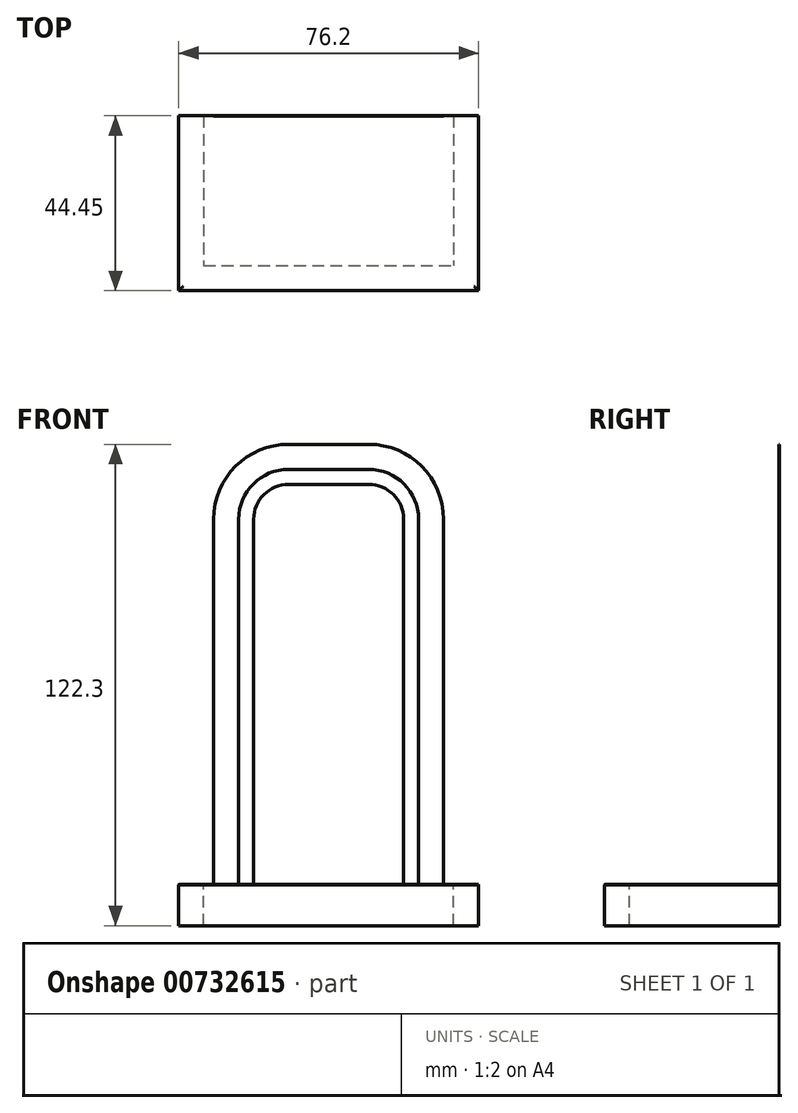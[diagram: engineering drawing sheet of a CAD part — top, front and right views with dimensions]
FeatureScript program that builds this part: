
annotation { "Feature Type Name" : "Feature", "Feature Type Description" : "" }
export const myFeature = defineFeature(function(context is Context, id is Id, definition is map)
    precondition{}
    {
        {
            assignVariable(context, id + "F0", {"name" : "t", "anyValue" : .125});
        }
        {
            var Q0;
            Q0=qCreatedBy(makeId("Front.planeOp"),FACE);
            var sketch = newSketch(context, id + "F1", { "sketchPlane" : qUnion([Q0])});
            skLineSegment(sketch, "E0.bottom", {"start": v(19.05, 111.76) * mm, "end": v(39.37, 111.76) * mm});
            skLineSegment(sketch, "E0.top", {"start": v(0, 0) * mm, "end": v(6.35, 0) * mm});
            skLineSegment(sketch, "E0.left", {"start": v(0, 92.71) * mm, "end": v(0, 0) * mm});
            skLineSegment(sketch, "E0.right", {"start": v(58.42, 92.71) * mm, "end": v(58.42, 0) * mm});
            skPoint(sketch, "E1.visualSharp", {"position": v(0, 111.76) * mm});
            skArc(sketch, "E1.filletArc", {"start": v(19.05, 111.76) * mm, "mid": v(5.58, 106.18) * mm, "end": v(0, 92.71) * mm});
            skPoint(sketch, "E2.visualSharp", {"position": v(58.42, 111.76) * mm});
            skArc(sketch, "E2.filletArc", {"start": v(58.42, 92.71) * mm, "mid": v(52.84, 106.18) * mm, "end": v(39.37, 111.76) * mm});
            skLineSegment(sketch, "E3.0", {"start": v(52.07, 92.71) * mm, "end": v(52.07, 0) * mm});
            skLineSegment(sketch, "E3.1", {"start": v(6.35, 92.71) * mm, "end": v(6.35, 0) * mm});
            skArc(sketch, "E3.2", {"start": v(19.05, 105.41) * mm, "mid": v(10.07, 101.7) * mm, "end": v(6.35, 92.71) * mm});
            skLineSegment(sketch, "E3.3", {"start": v(19.05, 105.41) * mm, "end": v(39.37, 105.41) * mm});
            skArc(sketch, "E3.4", {"start": v(52.07, 92.71) * mm, "mid": v(48.35, 101.7) * mm, "end": v(39.37, 105.41) * mm});
            skLineSegment(sketch, "E4.trimOffspring", {"start": v(52.07, 0) * mm, "end": v(58.42, 0) * mm});
            skSolve(sketch);
        }
        {
            var Q0;
            Q0 = qSketchRegion(id + "F1", true);
            extrude(context, id + "F2", {"entities" : qUnion([Q0]), "depth" : (getVariable(context, 't')) * mm, "offsetDistance" : 25.4 * mm});
        }
        {
            var Q0;
            Q0=qCreatedBy(makeId("Top.planeOp"),FACE);
            var sketch = newSketch(context, id + "F3", { "sketchPlane" : qUnion([Q0])});
            skLineSegment(sketch, "E5.bottom", {"start": v(-8.9, 0) * mm, "end": v(67.3, 0) * mm});
            skLineSegment(sketch, "E5.top", {"start": v(-8.9, -44.45) * mm, "end": v(67.3, -44.45) * mm});
            skLineSegment(sketch, "E5.left", {"start": v(-8.9, 0) * mm, "end": v(-8.9, -44.45) * mm});
            skLineSegment(sketch, "E5.right", {"start": v(67.3, 0) * mm, "end": v(67.31, -44.45) * mm});
            skPoint(sketch, "E6", {"position": v(29.2, 0) * mm});
            skSolve(sketch);
        }
        {
            var Q0;
            Q0 = qSketchRegion(id + "F3", true);
            extrude(context, id + "F4", {"entities" : qUnion([Q0]), "operationType" : NewBodyOperationType.ADD, "oppositeDirection" : true, "depth" : (getVariable(context, 't')) * mm, "offsetDistance" : 25.4 * mm});
        }
        {
            var Q0;
            Q0=qCreatedBy(makeId("Front.planeOp"),FACE);
            var sketch = newSketch(context, id + "F5", { "sketchPlane" : qUnion([Q0])});
            skLineSegment(sketch, "E7.bottom", {"start": v(19.05, 101.6) * mm, "end": v(39.37, 101.6) * mm});
            skLineSegment(sketch, "E7.top", {"start": v(10.16, 0) * mm, "end": v(48.26, 0) * mm});
            skLineSegment(sketch, "E7.left", {"start": v(10.16, 92.71) * mm, "end": v(10.16, 0) * mm});
            skLineSegment(sketch, "E7.right", {"start": v(48.26, 92.71) * mm, "end": v(48.26, 0) * mm});
            skPoint(sketch, "E8.visualSharp", {"position": v(10.16, 101.6) * mm});
            skArc(sketch, "E8.filletArc", {"start": v(19.05, 101.6) * mm, "mid": v(12.76, 99) * mm, "end": v(10.16, 92.71) * mm});
            skPoint(sketch, "E9.visualSharp", {"position": v(48.26, 101.6) * mm});
            skArc(sketch, "E9.filletArc", {"start": v(48.26, 92.71) * mm, "mid": v(45.66, 99) * mm, "end": v(39.37, 101.6) * mm});
            skPoint(sketch, "E10", {"position": v(29.21, 0) * mm});
            skLineSegment(sketch, "E11.0.1", {"start": v(58.42, 0) * mm, "end": v(52.07, 0) * mm});
            skLineSegment(sketch, "E11.0.3", {"start": v(52.07, 0) * mm, "end": v(6.35, 0) * mm});
            skLineSegment(sketch, "E11.0.5", {"start": v(6.35, 0) * mm, "end": v(0, 0) * mm});
            skLineSegment(sketch, "E11.0.7", {"start": v(0, 0) * mm, "end": v(-8.9, 0) * mm});
            skLineSegment(sketch, "E11.0.9", {"start": v(-8.9, 0) * mm, "end": v(67.31, 0) * mm});
            skLineSegment(sketch, "E11.0.11", {"start": v(67.3, 0) * mm, "end": v(58.42, 0) * mm});
            skSolve(sketch);
        }
        {
            var Q0;
            Q0=makeQuery(id+"F5.imprint","IMPRINT",FACE,{"disambiguationData":[TD([[makeQuery(id+"F5.imprint","IMPRINT",EDGE,{"derivedFrom":sQuery(id+"F5.wireOp",EDGE,"E7.bottom")}),-1.0]])]});
            extrude(context, id + "F6", {"entities" : qUnion([Q0]), "operationType" : NewBodyOperationType.ADD, "depth" : (getVariable(context, 't')) * mm, "offsetDistance" : 25.4 * mm});
        }
        {
            var Q0;
            Q0=qCreatedBy(makeId("Top.planeOp"),FACE);
            var sketch = newSketch(context, id + "F7", { "sketchPlane" : qUnion([Q0])});
            skLineSegment(sketch, "E12.bottom", {"start": v(-8.9, 0) * mm, "end": v(-2.54, 0) * mm});
            skLineSegment(sketch, "E12.top", {"start": v(-8.9, -44.45) * mm, "end": v(67.3, -44.45) * mm});
            skLineSegment(sketch, "E12.left", {"start": v(-8.9, 0) * mm, "end": v(-8.9, -44.45) * mm});
            skLineSegment(sketch, "E12.right", {"start": v(67.3, 0) * mm, "end": v(67.3, -44.45) * mm});
            skLineSegment(sketch, "E13.0", {"start": v(-2.54, 0) * mm, "end": v(-2.54, -38.1) * mm});
            skLineSegment(sketch, "E13.1", {"start": v(-2.54, -38.1) * mm, "end": v(60.96, -38.1) * mm});
            skLineSegment(sketch, "E13.2", {"start": v(60.96, 0) * mm, "end": v(60.96, -38.1) * mm});
            skLineSegment(sketch, "E14.trimOffspring", {"start": v(60.96, 0) * mm, "end": v(67.3, 0) * mm});
            skLineSegment(sketch, "E15.0.0", {"start": v(-8.9, -44.45) * mm, "end": v(-8.9, 0) * mm});
            skLineSegment(sketch, "E15.0.1", {"start": v(-8.9, 0) * mm, "end": v(67.3, 0) * mm});
            skLineSegment(sketch, "E15.0.2", {"start": v(67.31, 0) * mm, "end": v(67.31, -44.45) * mm});
            skLineSegment(sketch, "E15.0.3", {"start": v(67.31, -44.45) * mm, "end": v(-8.9, -44.45) * mm});
            skSolve(sketch);
        }
        {
            var Q0;
            Q0=makeQuery(id+"F7.imprint","IMPRINT",FACE,{"disambiguationData":[TD([[makeQuery(id+"F7.imprint","IMPRINT",EDGE,{"derivedFrom":sQuery(id+"F7.wireOp",EDGE,"E12.bottom")}),-1.0]])]});
            var Q1;
            {var subQ2=sQuery(id+"F7.wireOp",EDGE,"E13.0");Q1=makeQuery(id+"F7.imprint","IMPRINT",FACE,{"disambiguationData":[TD([[makeQuery(id+"F7.imprint","IMPRINT",EDGE,{"derivedFrom":subQ2}),-1.0]])]});}
            extrude(context, id + "F8", {"entities" : qUnion([Q0, Q1]), "oppositeDirection" : true, "depth" : 10.4 * mm, "offsetDistance" : 25.4 * mm});
        }
        {
            var Q0;
            Q0=makeQuery(id+"F8.opExtrude","SWEPT_BODY",BODY,{"disambiguationData":[OSD([sQuery(id+"F7.wireOp",EDGE,"E12.bottom"),sQuery(id+"F7.wireOp",EDGE,"E13.0"),sQuery(id+"F7.wireOp",EDGE,"E13.1"),sQuery(id+"F7.wireOp",EDGE,"E13.2"),sQuery(id+"F7.wireOp",EDGE,"E14.trimOffspring"),sQuery(id+"F7.wireOp",EDGE,"E15.0.0"),sQuery(id+"F7.wireOp",EDGE,"E15.0.2"),sQuery(id+"F7.wireOp",EDGE,"E15.0.3")])]});
            transform(context, id + "F9", {"entities" : qUnion([Q0]), "transformType" : TransformType.TRANSLATION_3D, "dx" : 0 * mm, "dy" : 0 * mm, "dz" : (-getVariable(context, 't')) * mm, "makeCopy" : false});
        }
        {
            var Q0;
            Q0=makeQuery(id+"F4.opExtrude","CAP_EDGE",EDGE,{"disambiguationData":[OSD([sQuery(id+"F3.wireOp",EDGE,"E5.top")])],"isStart":true});
            var Q1;
            Q1=makeQuery(id+"F4.opExtrude","CAP_EDGE",EDGE,{"disambiguationData":[OSD([sQuery(id+"F3.wireOp",EDGE,"E5.right")])],"isStart":true});
            var Q2;
            Q2=makeQuery(id+"F4.opExtrude","CAP_EDGE",EDGE,{"disambiguationData":[OSD([sQuery(id+"F3.wireOp",EDGE,"E5.left")])],"isStart":true});
            fillet(context, id + "F10", {"entities" : qUnion([Q0, Q1, Q2]), "radius" : 5.08 * mm, "tangentPropagation" : true, "allowEdgeOverflow" : false});
        }
    });
